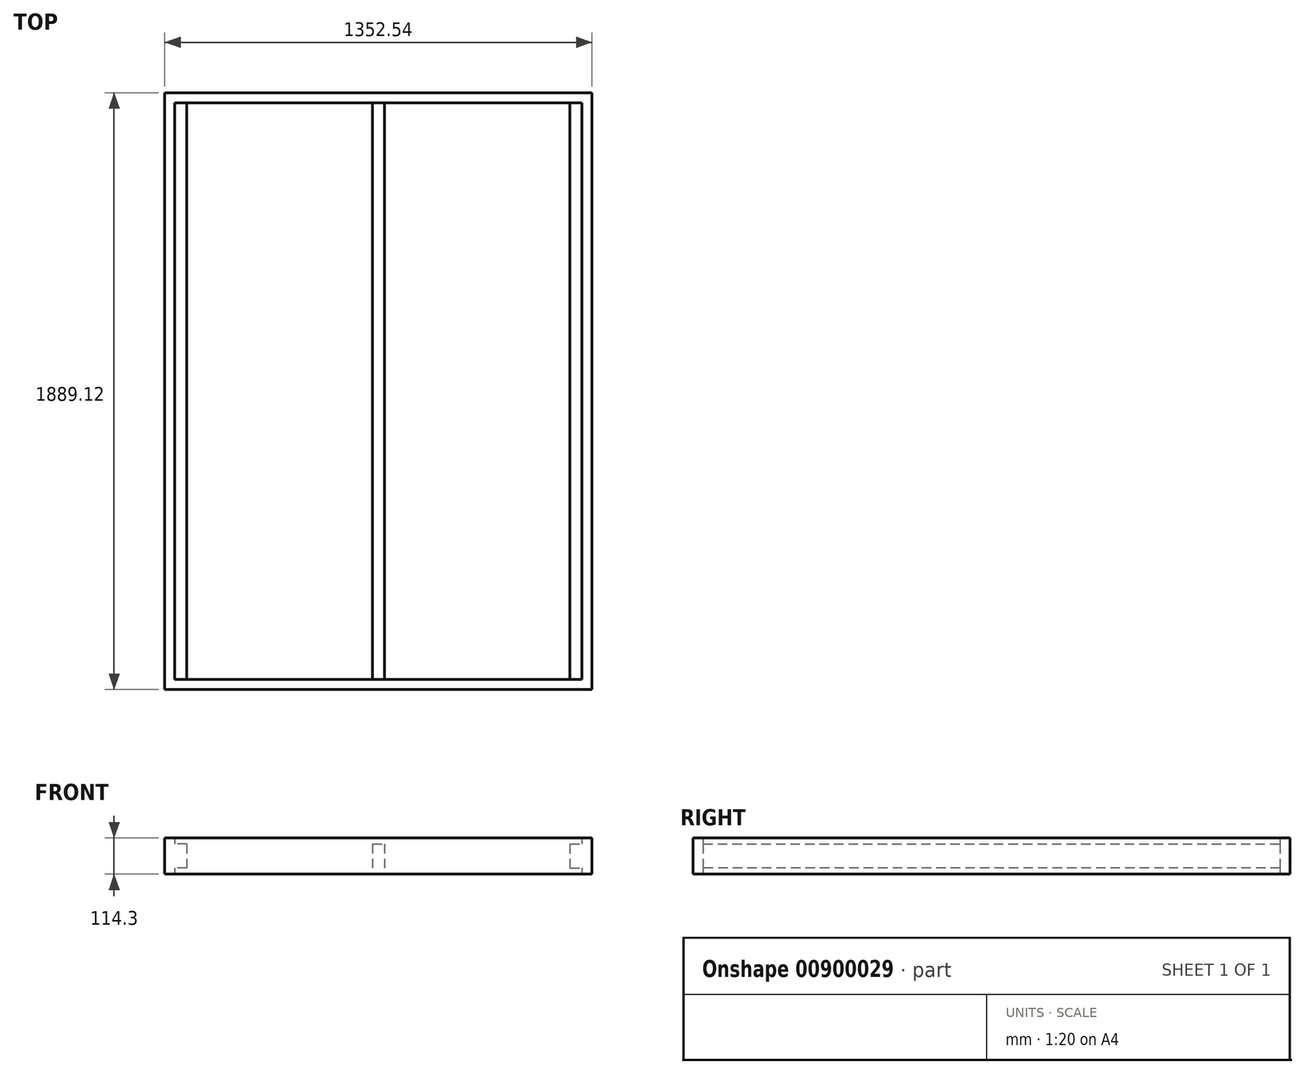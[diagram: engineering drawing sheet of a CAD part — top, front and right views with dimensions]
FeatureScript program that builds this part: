
annotation { "Feature Type Name" : "Feature", "Feature Type Description" : "" }
export const myFeature = defineFeature(function(context is Context, id is Id, definition is map)
    precondition{}
    {
        {
            var Q0;
            Q0=qCreatedBy(makeId("Top.planeOp"),FACE);
            var sketch = newSketch(context, id + "F0", { "sketchPlane" : qUnion([Q0])});
            skLineSegment(sketch, "E0.bottom", {"start": v(676.28, -944.56) * mm, "end": v(-676.27, -944.56) * mm});
            skLineSegment(sketch, "E0.top", {"start": v(676.27, 944.56) * mm, "end": v(-676.28, 944.56) * mm});
            skLineSegment(sketch, "E0.left", {"start": v(676.28, -944.56) * mm, "end": v(676.27, 944.56) * mm});
            skLineSegment(sketch, "E0.right", {"start": v(-676.27, -944.56) * mm, "end": v(-676.28, 944.56) * mm});
            skPoint(sketch, "E0.middle", {"position": v(0, 0) * mm});
            skLineSegment(sketch, "E1.bottom", {"start": v(644.52, 912.81) * mm, "end": v(-644.53, 912.81) * mm});
            skLineSegment(sketch, "E1.top", {"start": v(644.53, -912.81) * mm, "end": v(-644.52, -912.81) * mm});
            skLineSegment(sketch, "E1.left", {"start": v(644.52, 912.81) * mm, "end": v(644.53, -912.81) * mm});
            skLineSegment(sketch, "E1.right", {"start": v(-644.53, 912.81) * mm, "end": v(-644.52, -912.81) * mm});
            skSolve(sketch);
        }
        {
            var Q0;
            Q0=makeQuery(id+"F0.imprint","IMPRINT",FACE,{"disambiguationData":[TD([[makeQuery(id+"F0.imprint","IMPRINT",EDGE,{"derivedFrom":sQuery(id+"F0.wireOp",EDGE,"E0.bottom")}),-1.0]])]});
            extrude(context, id + "F1", {"entities" : qUnion([Q0]), "depth" : 114.3 * mm, "offsetDistance" : 25.4 * mm});
        }
        {
            var Q0;
            Q0=makeQuery(id+"F1.opExtrude","SWEPT_FACE",FACE,{"disambiguationData":[OSD([sQuery(id+"F0.wireOp",EDGE,"E1.right")])]});
            var sketch = newSketch(context, id + "F2", { "sketchPlane" : qUnion([Q0])});
            skLineSegment(sketch, "E2.bottom", {"start": v(912.81, 95.25) * mm, "end": v(-912.81, 95.25) * mm});
            skLineSegment(sketch, "E2.top", {"start": v(912.81, 19.05) * mm, "end": v(-912.81, 19.05) * mm});
            skLineSegment(sketch, "E2.left", {"start": v(912.81, 95.25) * mm, "end": v(912.81, 19.05) * mm});
            skLineSegment(sketch, "E2.right", {"start": v(-912.81, 95.25) * mm, "end": v(-912.81, 19.05) * mm});
            skSolve(sketch);
        }
        {
            var Q0;
            Q0 = qSketchRegion(id + "F2", true);
            extrude(context, id + "F3", {"entities" : qUnion([Q0]), "operationType" : NewBodyOperationType.ADD, "depth" : 38.1 * mm, "offsetDistance" : 25.4 * mm});
        }
        {
            var Q0;
            Q0=makeQuery(id+"F1.opExtrude","SWEPT_FACE",FACE,{"disambiguationData":[OSD([sQuery(id+"F0.wireOp",EDGE,"E1.left")])]});
            var sketch = newSketch(context, id + "F4", { "sketchPlane" : qUnion([Q0])});
            skLineSegment(sketch, "E3.bottom", {"start": v(912.81, 19.05) * mm, "end": v(-912.81, 19.05) * mm});
            skLineSegment(sketch, "E3.top", {"start": v(912.81, 95.25) * mm, "end": v(-912.81, 95.25) * mm});
            skLineSegment(sketch, "E3.left", {"start": v(912.81, 19.05) * mm, "end": v(912.81, 95.25) * mm});
            skLineSegment(sketch, "E3.right", {"start": v(-912.81, 19.05) * mm, "end": v(-912.81, 95.25) * mm});
            skSolve(sketch);
        }
        {
            var Q0;
            Q0 = qSketchRegion(id + "F4", true);
            extrude(context, id + "F5", {"entities" : qUnion([Q0]), "operationType" : NewBodyOperationType.ADD, "depth" : 38.1 * mm, "offsetDistance" : 25.4 * mm});
        }
        {
            var Q0;
            Q0=makeQuery(id+"F1.opExtrude","SWEPT_FACE",FACE,{"disambiguationData":[OSD([sQuery(id+"F0.wireOp",EDGE,"E1.bottom")])]});
            var sketch = newSketch(context, id + "F6", { "sketchPlane" : qUnion([Q0])});
            skLineSegment(sketch, "E4.left", {"start": v(19.05, 95.25) * mm, "end": v(19.05, 0) * mm});
            skLineSegment(sketch, "E4.right", {"start": v(-19.05, 95.25) * mm, "end": v(-19.05, 0) * mm});
            skPoint(sketch, "E4.middle", {"position": v(0, 114.3) * mm});
            skLineSegment(sketch, "E5.bottom", {"start": v(-19.05, 0) * mm, "end": v(19.05, 0) * mm});
            skLineSegment(sketch, "E5.top", {"start": v(-19.05, 95.25) * mm, "end": v(19.05, 95.25) * mm});
            skLineSegment(sketch, "E5.left", {"start": v(-19.05, 0) * mm, "end": v(-19.05, 95.25) * mm});
            skLineSegment(sketch, "E5.right", {"start": v(19.05, 0) * mm, "end": v(19.05, 95.25) * mm});
            skPoint(sketch, "E6.orphan", {"position": v(-19.05, 264.73) * mm});
            skPoint(sketch, "E7.orphan", {"position": v(19.05, 264.73) * mm});
            skPoint(sketch, "E4.top.end.orphan", {"position": v(-19.05, -36.13) * mm});
            skPoint(sketch, "E8.orphan", {"position": v(19.05, -36.13) * mm});
            skSolve(sketch);
        }
        {
            var Q0;
            Q0 = qSketchRegion(id + "F6", true);
            extrude(context, id + "F7", {"entities" : qUnion([Q0]), "operationType" : NewBodyOperationType.ADD, "endBound" : BoundingType.UP_TO_NEXT, "depth" : 25.4 * mm, "offsetDistance" : 25.4 * mm});
        }
    });
